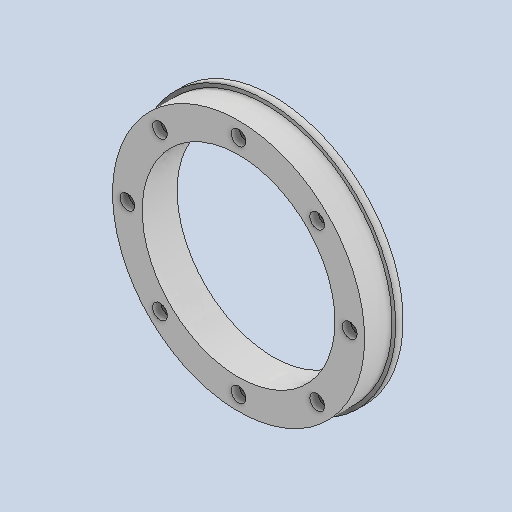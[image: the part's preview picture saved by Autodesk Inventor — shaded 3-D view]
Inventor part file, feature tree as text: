
AUTODESK INVENTOR PART (.ipt)
format: ipt  version: 2024.2 (Build 282272000, 272)  size: 168,960 bytes
history: native  units: mm
features: extrude x4, sketch x4, pattern_circular x1, projected_geometry x1
ambient origin geometry x8: Origin, YZ Plane, XZ Plane, XY Plane, X Axis, Y Axis, Z Axis, Center Point
bodies: Solid1 (feature_tree)
feature tree (10):
  extrude  "Extrusion1"  Depth=260.0mm
  extrude  "Extrusion2"  Depth=47.0mm
  extrude  "Extrusion3"  Depth=80.0mm TaperAngle=360.0deg
  pattern_circular  "Circular Pattern1"  Count=2  [1 undecoded]
  extrude  "Extrusion4"  Depth=10.0mm
  sketch  "Sketch1"  dims[d0=40.0mm d1=260.0mm]
  sketch  "Sketch2"  dims[d2=47.0mm d3=0.0mm d4=12.5mm]
  projected_geometry  "Projected Loop1"
  sketch  "Sketch3"  dims[d5=0.0mm d6=0.0mm d7=80.0mm d8=360.0deg d10=20.0mm]
  sketch  "Sketch4"  dims[d11=11.0mm d12=0.0mm d13=5.0mm d14=10.0mm d15=0.0mm]
note: 1 required parameter value undecoded (feature->parameter linkage not recoverable at this tier; creation-order binding heuristic only, values carry confidence <= 0.55)
